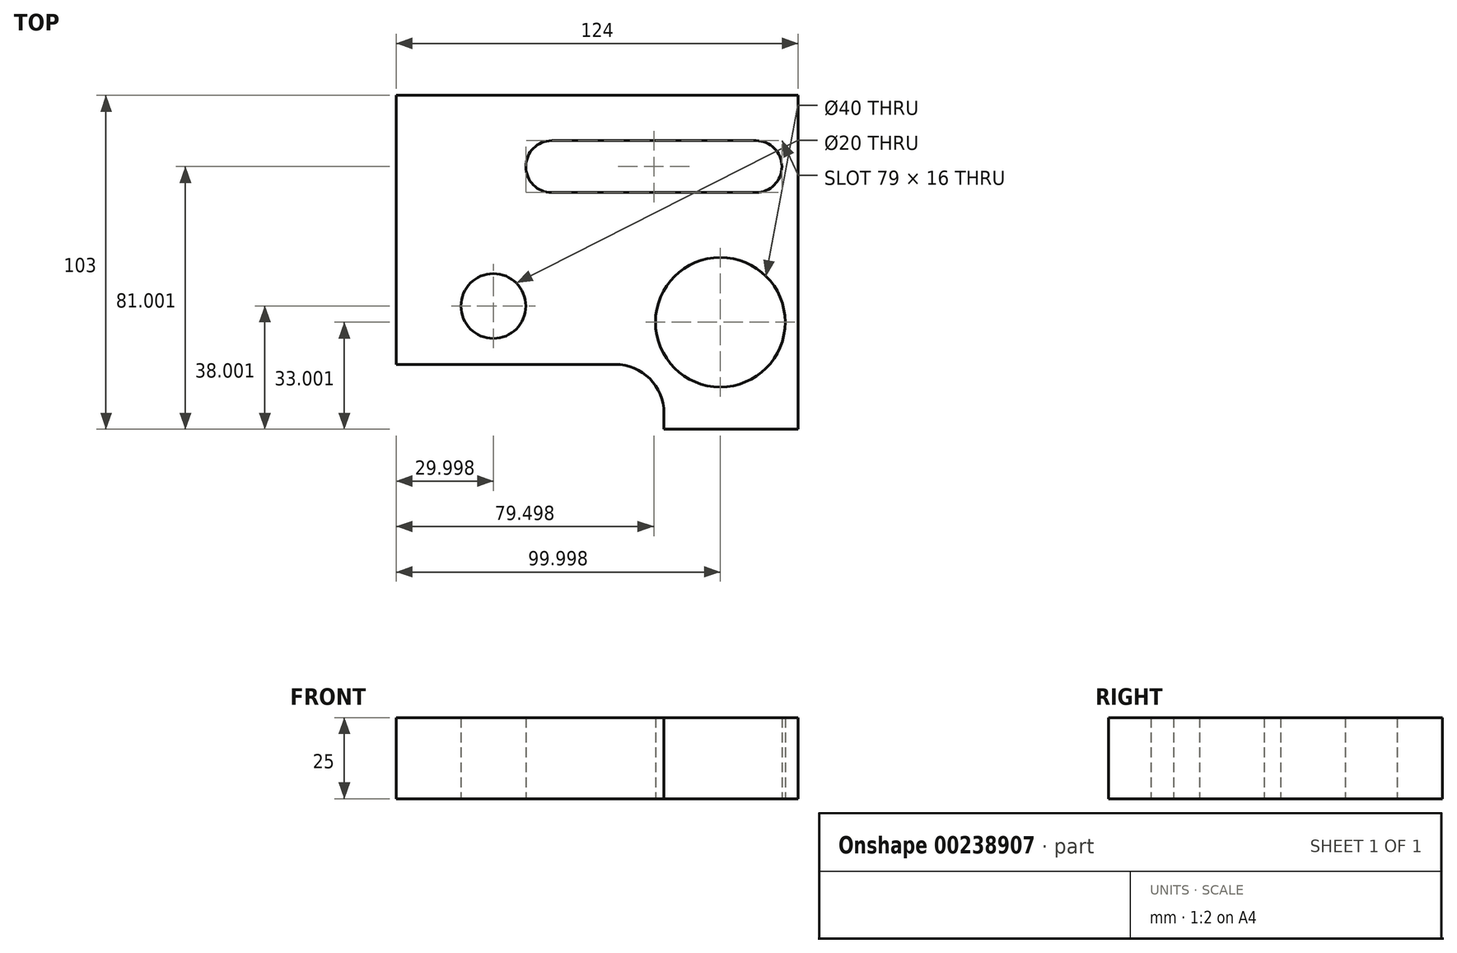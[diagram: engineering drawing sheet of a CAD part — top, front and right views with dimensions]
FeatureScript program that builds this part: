
annotation { "Feature Type Name" : "Feature", "Feature Type Description" : "" }
export const myFeature = defineFeature(function(context is Context, id is Id, definition is map)
    precondition{}
    {
        {
            var Q0;
            Q0=qCreatedBy(makeId("Top.planeOp"),FACE);
            var sketch = newSketch(context, id + "F0", { "sketchPlane" : qUnion([Q0])});
            skLineSegment(sketch, "E0", {"start": v(67.26, -67.92) * mm, "end": v(67.26, 35.08) * mm});
            skLineSegment(sketch, "E1", {"start": v(67.26, 35.08) * mm, "end": v(-56.74, 35.08) * mm});
            skLineSegment(sketch, "E2", {"start": v(-56.74, 35.08) * mm, "end": v(-56.74, -47.92) * mm});
            skLineSegment(sketch, "E3", {"start": v(-56.74, -47.92) * mm, "end": v(10.87, -47.92) * mm});
            skLineSegment(sketch, "E4", {"start": v(25.87, -62.92) * mm, "end": v(25.87, -67.92) * mm});
            skLineSegment(sketch, "E5", {"start": v(25.87, -67.92) * mm, "end": v(67.26, -67.92) * mm});
            skPoint(sketch, "E6.visualSharp", {"position": v(25.87, -47.92) * mm});
            skArc(sketch, "E6.filletArc", {"start": v(25.87, -62.92) * mm, "mid": v(21.48, -52.31) * mm, "end": v(10.87, -47.92) * mm});
            skLineSegment(sketch, "E7", {"start": v(-56.74, -47.92) * mm, "end": v(-26.74, -47.92) * mm, "construction": true});
            skLineSegment(sketch, "E8", {"start": v(-26.74, -47.92) * mm, "end": v(-26.74, -29.92) * mm, "construction": true});
            skLineSegment(sketch, "E9", {"start": v(-56.74, 35.08) * mm, "end": v(43.26, 35.08) * mm});
            skLineSegment(sketch, "E10", {"start": v(43.26, 35.08) * mm, "end": v(43.26, -34.92) * mm, "construction": true});
            skLineSegment(sketch, "E11", {"start": v(67.26, 35.08) * mm, "end": v(-16.74, 35.08) * mm, "construction": true});
            skLineSegment(sketch, "E12", {"start": v(-16.74, 35.08) * mm, "end": v(-16.74, 21.08) * mm, "construction": true});
            skLineSegment(sketch, "E13", {"start": v(-16.74, 13.08) * mm, "end": v(-16.74, 13.08) * mm});
            skLineSegment(sketch, "E14", {"start": v(-8.74, 5.08) * mm, "end": v(54.26, 5.08) * mm});
            skLineSegment(sketch, "E15", {"start": v(62.26, 13.08) * mm, "end": v(62.26, 13.08) * mm});
            skCircle(sketch, "E16", {"center": v(-26.74, -29.92) * mm, "radius": 10 * mm});
            skCircle(sketch, "E17", {"center": v(43.26, -34.92) * mm, "radius": 20 * mm});
            skLineSegment(sketch, "E18", {"start": v(-8.74, 21.08) * mm, "end": v(54.26, 21.08) * mm});
            skPoint(sketch, "E19.visualSharp", {"position": v(-16.74, 21.08) * mm});
            skArc(sketch, "E19.filletArc", {"start": v(-8.74, 21.08) * mm, "mid": v(-14.4, 18.74) * mm, "end": v(-16.74, 13.08) * mm});
            skPoint(sketch, "E20.visualSharp", {"position": v(-16.74, 5.08) * mm});
            skArc(sketch, "E20.filletArc", {"start": v(-16.74, 13.08) * mm, "mid": v(-14.4, 7.42) * mm, "end": v(-8.74, 5.08) * mm});
            skPoint(sketch, "E21.visualSharp", {"position": v(62.26, 21.08) * mm});
            skArc(sketch, "E21.filletArc", {"start": v(62.26, 13.08) * mm, "mid": v(59.92, 18.74) * mm, "end": v(54.26, 21.08) * mm});
            skPoint(sketch, "E22.visualSharp", {"position": v(62.26, 5.08) * mm});
            skArc(sketch, "E22.filletArc", {"start": v(54.26, 5.08) * mm, "mid": v(59.92, 7.42) * mm, "end": v(62.26, 13.08) * mm});
            skLineSegment(sketch, "E23", {"start": v(62.26, 5.08) * mm, "end": v(67.26, 5.08) * mm});
            skSolve(sketch);
        }
        {
            var Q0;
            Q0 = qSketchRegion(id + "F0", true);
            extrude(context, id + "F1", {"entities" : qUnion([Q0]), "depth" : 25 * mm});
        }
    });
